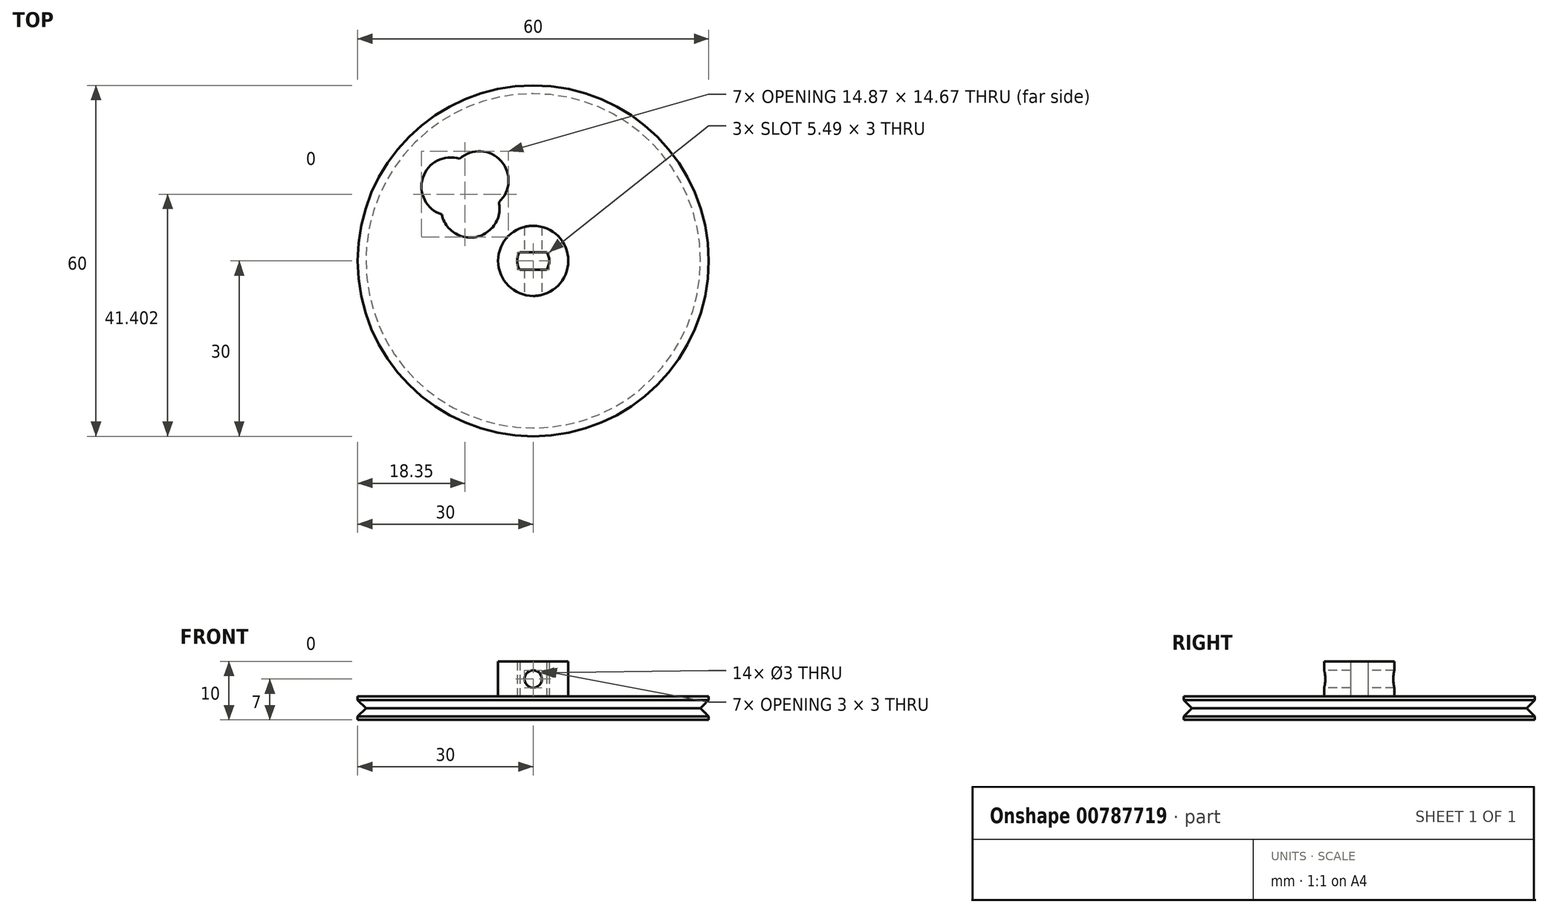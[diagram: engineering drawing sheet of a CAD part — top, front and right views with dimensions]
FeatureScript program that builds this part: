
annotation { "Feature Type Name" : "Feature", "Feature Type Description" : "" }
export const myFeature = defineFeature(function(context is Context, id is Id, definition is map)
    precondition{}
    {
        {
            var Q0;
            Q0=qCreatedBy(makeId("Top.planeOp"),FACE);
            var sketch = newSketch(context, id + "F0", { "sketchPlane" : qUnion([Q0])});
            skCircle(sketch, "E0", {"center": v(0, 0) * mm, "radius": 30 * mm});
            skCircle(sketch, "E1", {"center": v(0, 0) * mm, "radius": 6 * mm});
            skLineSegment(sketch, "E2", {"start": v(0, 38.2) * mm, "end": v(0, -41.43) * mm, "construction": true});
            skSolve(sketch);
        }
        {
            var Q0;
            Q0=makeQuery(id+"F0.imprint","IMPRINT",FACE,{"disambiguationData":[TD([[makeQuery(id+"F0.imprint","IMPRINT",EDGE,{"derivedFrom":sQuery(id+"F0.wireOp",EDGE,"E1")}),1.0]])]});
            var Q1;
            Q1=makeQuery(id+"F0.imprint","IMPRINT",FACE,{"disambiguationData":[TD([[makeQuery(id+"F0.imprint","IMPRINT",EDGE,{"derivedFrom":sQuery(id+"F0.wireOp",EDGE,"E0")}),1.0]])]});
            extrude(context, id + "F1", {"entities" : qUnion([Q0, Q1]), "oppositeDirection" : true, "depth" : 4 * mm, "offsetDistance" : 25 * mm});
        }
        {
            var Q0;
            Q0=makeQuery(id+"F0.imprint","IMPRINT",FACE,{"disambiguationData":[TD([[makeQuery(id+"F0.imprint","IMPRINT",EDGE,{"derivedFrom":sQuery(id+"F0.wireOp",EDGE,"E1")}),1.0]])]});
            extrude(context, id + "F2", {"entities" : qUnion([Q0]), "operationType" : NewBodyOperationType.ADD, "depth" : 6 * mm, "offsetDistance" : 25 * mm});
        }
        {
            var Q0;
            Q0=qCreatedBy(makeId("Front.planeOp"),FACE);
            var sketch = newSketch(context, id + "F3", { "sketchPlane" : qUnion([Q0])});
            skCircle(sketch, "E3", {"center": v(0, 3) * mm, "radius": 1.5 * mm});
            skSolve(sketch);
        }
        {
            var Q0;
            Q0 = qSketchRegion(id + "F3", true);
            extrude(context, id + "F4", {"entities" : qUnion([Q0]), "operationType" : NewBodyOperationType.REMOVE, "endBound" : BoundingType.SYMMETRIC, "oppositeDirection" : true, "depth" : 25 * mm, "offsetDistance" : 25 * mm});
        }
        {
            var Q0;
            Q0=qCreatedBy(makeId("Top.planeOp"),FACE);
            var sketch = newSketch(context, id + "F5", { "sketchPlane" : qUnion([Q0])});
            skLineSegment(sketch, "E4.bottom", {"start": v(-2.3, -1.5) * mm, "end": v(2.3, -1.5) * mm});
            skLineSegment(sketch, "E4.top", {"start": v(-2.3, 1.5) * mm, "end": v(2.3, 1.5) * mm});
            skLineSegment(sketch, "E4.left", {"start": v(-2.3, -1.5) * mm, "end": v(-2.3, 1.5) * mm});
            skLineSegment(sketch, "E4.right", {"start": v(2.3, -1.5) * mm, "end": v(2.3, 1.5) * mm});
            skPoint(sketch, "E4.middle", {"position": v(0, 0) * mm});
            skArc(sketch, "E5", {"start": v(2.3, -1.5) * mm, "mid": v(2.75, 0) * mm, "end": v(2.3, 1.5) * mm});
            skArc(sketch, "E6", {"start": v(-2.3, 1.5) * mm, "mid": v(-2.75, 0) * mm, "end": v(-2.3, -1.5) * mm});
            skSolve(sketch);
        }
        {
            var Q0;
            Q0 = qSketchRegion(id + "F5", true);
            extrude(context, id + "F6", {"entities" : qUnion([Q0]), "operationType" : NewBodyOperationType.REMOVE, "depth" : 9.4 * mm, "offsetDistance" : 25 * mm});
        }
        {
            var Q0;
            Q0=qCreatedBy(makeId("Front.planeOp"),FACE);
            var sketch = newSketch(context, id + "F7", { "sketchPlane" : qUnion([Q0])});
            skLineSegment(sketch, "E7", {"start": v(-30, -4) * mm, "end": v(-30, 0) * mm});
            skLineSegment(sketch, "E8", {"start": v(-30, -4) * mm, "end": v(-30, 0) * mm, "construction": true});
            skLineSegment(sketch, "E9", {"start": v(-30, -0.59) * mm, "end": v(-28.59, -2) * mm});
            skLineSegment(sketch, "E10", {"start": v(-28.59, -2) * mm, "end": v(-30, -3.41) * mm});
            skLineSegment(sketch, "E11", {"start": v(-30, -2) * mm, "end": v(-26, -2) * mm, "construction": true});
            skLineSegment(sketch, "E12", {"start": v(0, 15) * mm, "end": v(0, -11.8) * mm, "construction": true});
            skSolve(sketch);
        }
        {
            var Q0;
            Q0=qCreatedBy(makeId("Top.planeOp"),FACE);
            var sketch = newSketch(context, id + "F8", { "sketchPlane" : qUnion([Q0])});
            skCircle(sketch, "E13", {"center": v(-14.1, 12.7) * mm, "radius": 5 * mm});
            skCircle(sketch, "E14", {"center": v(-9.21, 13.74) * mm, "radius": 5 * mm});
            skCircle(sketch, "E15", {"center": v(-10.74, 8.98) * mm, "radius": 5 * mm});
            skSolve(sketch);
        }
        {
            var Q0;
            Q0 = qSketchRegion(id + "F8", true);
            var Q1;
            {var subQ0=sQuery(id+"F8.wireOp",EDGE,"E15");var subQ1=sQuery(id+"F8.wireOp",EDGE,"E13");var subQ2=makeQuery(id+"F8.imprint","INTERSECT",VERTEX,{"disambiguationData":[OD(1.0)],"derivedFrom":[subQ1,subQ0]});Q1=makeQuery(id+"F8.imprint","IMPRINT",FACE,{"disambiguationData":[TD([[makeQuery(id+"F8.imprint","IMPRINT",EDGE,{"disambiguationData":[TD([[subQ2,1.0]])],"derivedFrom":subQ1}),1.0]])]});}
            extrude(context, id + "F9", {"entities" : qUnion([Q0, Q1]), "operationType" : NewBodyOperationType.REMOVE, "oppositeDirection" : true, "depth" : 45.7 * mm, "offsetDistance" : 25 * mm});
        }
        {
            var Q0;
            Q0 = qSketchRegion(id + "F7", true);
            var Q1;
            Q1=sQuery(id+"F7.wireOp",EDGE,"E12");
            revolve(context, id + "F10", {"operationType" : NewBodyOperationType.REMOVE, "surfaceOperationType" : NewSurfaceOperationType.NEW, "entities" : qUnion([Q0]), "axis" : qUnion([Q1]), "revolveType" : RevolveType.FULL});
        }
        {
            var Q0;
            Q0=makeQuery(id+"F1.opExtrude","SWEPT_BODY",BODY,{"disambiguationData":[OSD([sQuery(id+"F0.wireOp",EDGE,"E0")])]});
            var Q1;
            Q1=makeQuery(id+"F10.boolean.opBoolean","COPY",EDGE,{"derivedFrom":makeQuery(id+"F10.opRevolve","SWEPT_EDGE",EDGE,{"disambiguationData":[OSD([sQuery(id+"F7.wireOp",EDGE,"E7"),sQuery(id+"F7.wireOp",EDGE,"E10")])]})});
            circularPattern(context, id + "F11", {"entities" : qUnion([Q0]), "axis" : qUnion([Q1]), "angle" : 360 * degree, "instanceCount" : 4, "isCentered" : true});
        }
    });
